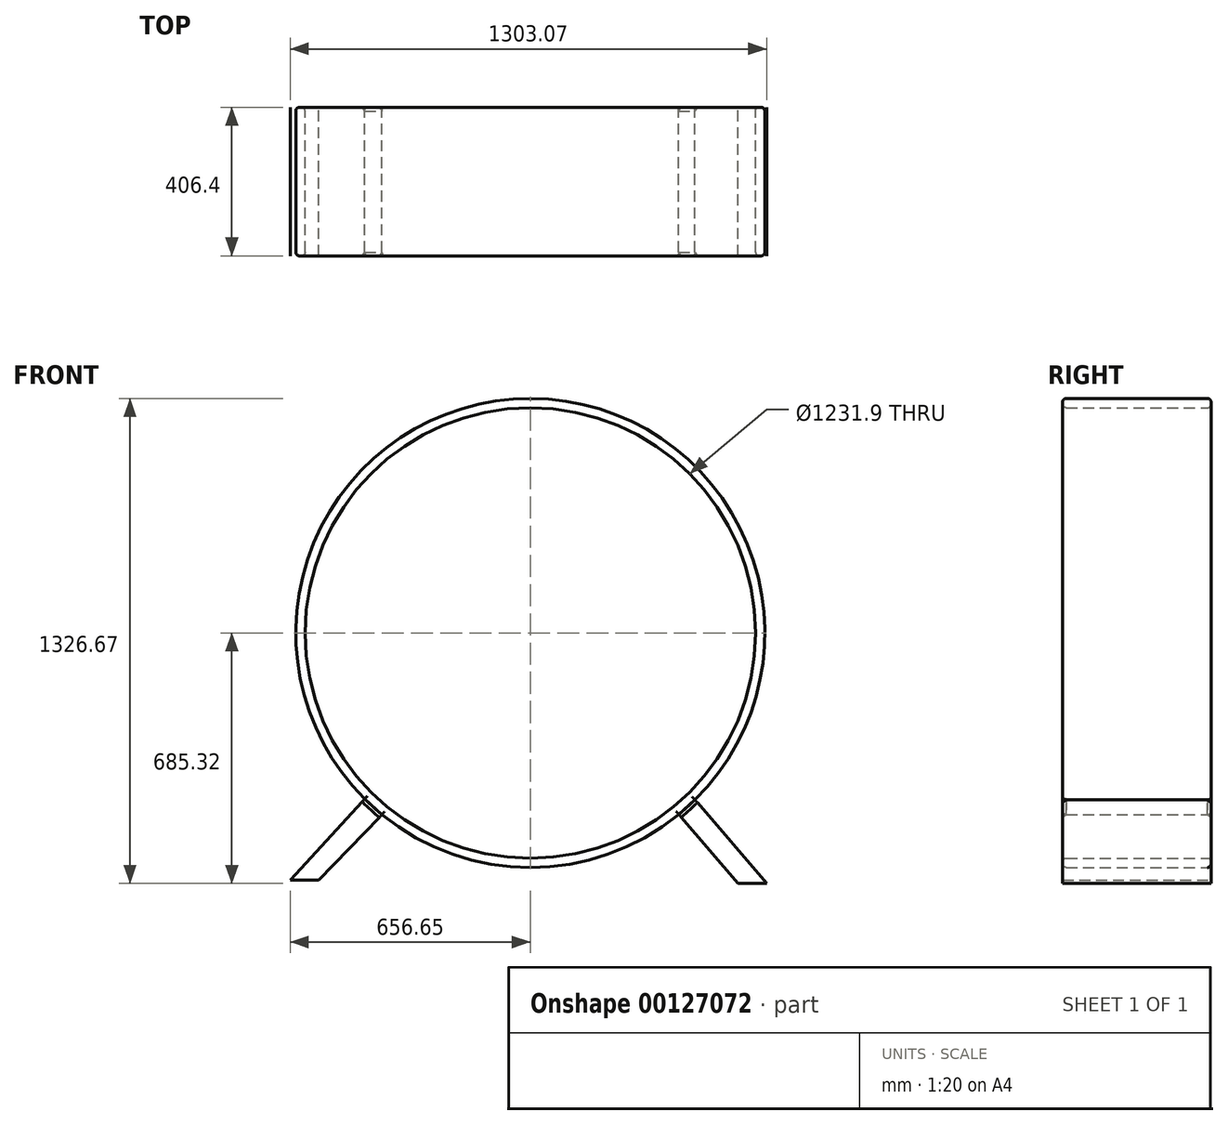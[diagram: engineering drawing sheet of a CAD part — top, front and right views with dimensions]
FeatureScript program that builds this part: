
annotation { "Feature Type Name" : "Feature", "Feature Type Description" : "" }
export const myFeature = defineFeature(function(context is Context, id is Id, definition is map)
    precondition{}
    {
        {
            var Q0;
            Q0=qCreatedBy(makeId("Front.planeOp"),FACE);
            var sketch = newSketch(context, id + "F0", { "sketchPlane" : qUnion([Q0])});
            skCircle(sketch, "E0", {"center": v(0, 0) * mm, "radius": 615.95 * mm});
            skCircle(sketch, "E1", {"center": v(0, 0) * mm, "radius": 641.35 * mm});
            skLineSegment(sketch, "E2", {"start": v(-405.83, -496.62) * mm, "end": v(-578.68, -675.98) * mm});
            skLineSegment(sketch, "E3", {"start": v(-578.68, -675.98) * mm, "end": v(-656.65, -675.98) * mm});
            skLineSegment(sketch, "E4", {"start": v(-656.65, -675.98) * mm, "end": v(-452.95, -454.06) * mm});
            skLineSegment(sketch, "E5", {"start": v(406.05, -496.44) * mm, "end": v(568.44, -685.32) * mm});
            skLineSegment(sketch, "E6", {"start": v(568.44, -685.32) * mm, "end": v(646.42, -685.32) * mm});
            skLineSegment(sketch, "E7", {"start": v(646.42, -685.32) * mm, "end": v(450.46, -456.53) * mm});
            skLineSegment(sketch, "E8", {"start": v(450.46, -456.53) * mm, "end": v(406.05, -496.44) * mm});
            skLineSegment(sketch, "E9", {"start": v(-452.95, -454.06) * mm, "end": v(-405.83, -496.62) * mm});
            skSolve(sketch);
        }
        {
            var Q0;
            Q0=makeQuery(id+"F0.imprint","IMPRINT",FACE,{"disambiguationData":[TD([[makeQuery(id+"F0.imprint","IMPRINT",EDGE,{"derivedFrom":sQuery(id+"F0.wireOp",EDGE,"E0")}),-1.0]])]});
            var Q1;
            {var subQ0=sQuery(id+"F0.wireOp",EDGE,"E2");Q1=makeQuery(id+"F0.imprint","IMPRINT",FACE,{"disambiguationData":[TD([[makeQuery(id+"F0.imprint","IMPRINT",EDGE,{"derivedFrom":subQ0}),-1.0]])]});}
            var Q2;
            {var subQ1=sQuery(id+"F0.wireOp",EDGE,"E5");Q2=makeQuery(id+"F0.imprint","IMPRINT",FACE,{"disambiguationData":[TD([[makeQuery(id+"F0.imprint","IMPRINT",EDGE,{"derivedFrom":subQ1}),1.0]])]});}
            extrude(context, id + "F1", {"entities" : qUnion([Q0, Q1, Q2]), "depth" : 406.4 * mm});
        }
        {
            var Q0;
            Q0=makeQuery(id+"F1.opExtrude","CAP_FACE",FACE,{"disambiguationData":[OSD([sQuery(id+"F0.wireOp",EDGE,"E0"),sQuery(id+"F0.wireOp",EDGE,"E1"),sQuery(id+"F0.wireOp",EDGE,"E8"),sQuery(id+"F0.wireOp",EDGE,"E9")])],"isStart":true});
            var Q1;
            Q1=makeQuery(id+"F1.opExtrude","CAP_FACE",FACE,{"disambiguationData":[OSD([sQuery(id+"F0.wireOp",EDGE,"E0"),sQuery(id+"F0.wireOp",EDGE,"E1"),sQuery(id+"F0.wireOp",EDGE,"E8"),sQuery(id+"F0.wireOp",EDGE,"E9")])],"isStart":false});
            fillet(context, id + "F2", {"entities" : qUnion([Q0, Q1]), "radius" : 10.16 * mm, "tangentPropagation" : true, "allowEdgeOverflow" : false});
        }
        {
            var Q0;
            {var subQ0=sQuery(id+"F0.wireOp",EDGE,"E8");var subQ1=sQuery(id+"F0.wireOp",EDGE,"E1");Q0=makeQuery(id+"F1.opExtrude","CAP_EDGE",EDGE,{"disambiguationData":[OSD([subQ1]),TDD([makeQuery(id+"F0.imprint","IMPRINT",EDGE,{"disambiguationData":[TD([[makeQuery(id+"F0.imprint","INTERSECT",VERTEX,{"derivedFrom":[subQ1,sQuery(id+"F0.wireOp",EDGE,"E5"),subQ0]}),-1.0]])],"derivedFrom":subQ1})])],"isStart":false});}
            var Q1;
            {var subQ0=sQuery(id+"F0.wireOp",EDGE,"E8");var subQ1=sQuery(id+"F0.wireOp",EDGE,"E1");Q1=makeQuery(id+"F1.opExtrude","CAP_EDGE",EDGE,{"disambiguationData":[OSD([subQ1]),TDD([makeQuery(id+"F0.imprint","IMPRINT",EDGE,{"disambiguationData":[TD([[makeQuery(id+"F0.imprint","INTERSECT",VERTEX,{"derivedFrom":[subQ1,sQuery(id+"F0.wireOp",EDGE,"E5"),subQ0]}),-1.0]])],"derivedFrom":subQ1})])],"isStart":true});}
            var Q2;
            {var subQ0=sQuery(id+"F0.wireOp",EDGE,"E9");var subQ1=sQuery(id+"F0.wireOp",EDGE,"E1");Q2=makeQuery(id+"F1.opExtrude","CAP_EDGE",EDGE,{"disambiguationData":[OSD([subQ1]),TDD([makeQuery(id+"F0.imprint","IMPRINT",EDGE,{"disambiguationData":[TD([[makeQuery(id+"F0.imprint","INTERSECT",VERTEX,{"derivedFrom":[subQ1,sQuery(id+"F0.wireOp",EDGE,"E2"),subQ0]}),1.0]])],"derivedFrom":subQ1})])],"isStart":false});}
            var Q3;
            {var subQ0=sQuery(id+"F0.wireOp",EDGE,"E9");var subQ1=sQuery(id+"F0.wireOp",EDGE,"E1");Q3=makeQuery(id+"F1.opExtrude","CAP_EDGE",EDGE,{"disambiguationData":[OSD([subQ1]),TDD([makeQuery(id+"F0.imprint","IMPRINT",EDGE,{"disambiguationData":[TD([[makeQuery(id+"F0.imprint","INTERSECT",VERTEX,{"derivedFrom":[subQ1,sQuery(id+"F0.wireOp",EDGE,"E2"),subQ0]}),1.0]])],"derivedFrom":subQ1})])],"isStart":true});}
            chamfer(context, id + "F3", {"entities" : qUnion([Q0, Q1, Q2, Q3]), "width" : 10.16 * mm, "tangentPropagation" : true});
        }
    });
